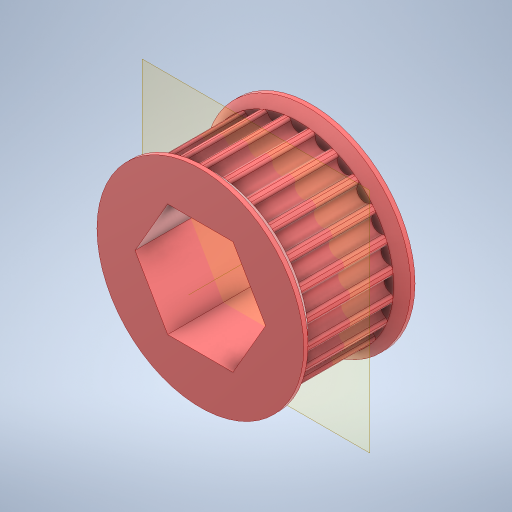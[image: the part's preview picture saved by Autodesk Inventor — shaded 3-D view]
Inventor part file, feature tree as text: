
AUTODESK INVENTOR PART (.ipt)
format: ipt  version: 2023.3 (Build 273359000, 359)  size: 504,832 bytes
history: native  units: in
note: dims shown in document units (in); Inventor stores cm internally (conversion verified against a paired STEP export)
features: sketch x7, extrude x6, mirror x2, chamfer x2, other x1, fillet x1, pattern_circular x1
ambient origin geometry x8: Origin, YZ Plane, XZ Plane, XY Plane, X Axis, Y Axis, Z Axis, Center Point
bodies: Solid1 (feature_tree)
feature tree (20):
  other  "Hex Bore"
  extrude  "HTD Base"  Depth=0.3937in TaperAngle=0.0deg
  extrude  "HTD Flange"  Depth=0.0591in
  mirror  "HTD Flanges"
  chamfer  "HTD Flange Chamfer"  Distance=0.0787in Angle=45.0deg
  extrude  "GT2 Base"  TaperAngle=0.0deg  [1 undecoded]
  extrude  "GT2 Base Tooth"  TaperAngle=0.0deg  [1 undecoded]
  fillet  "GT2 Base Tooth pt. 2"  Radius=0.8723in
  pattern_circular  "GT2 Teeth"  [2 undecoded]
  extrude  "GT2 Flange"  Depth=0.0591in
  mirror  "GT2 Flanges"
  chamfer  "GT2 Flange Chamfer"  Distance=0.0075in
  extrude  "Circle Bore"  TaperAngle=0.0deg  [1 undecoded]
  sketch  "Sketch1"  dims[d0=1.4588in d1=0.3937in d2=0.0in]
  sketch  "Sketch3"  dims[d12=0.0394in d13=0.0591in]
  sketch  "Sketch4"  dims[d14=0.0in]
  sketch  "Sketch5"  dims[d15=0.0394in d16=0.0787in d17=45.0deg]
  sketch  "Sketch6"  dims[d18=0.52in d19=0.0in d20=0.0in]
  sketch  "Sketch7"  dims[d21=0.52in d22=0.0in d23=0.0in d24=0.8723in]
  sketch  "Sketch8"  dims[d25=0.3937in d26=0.0in d27=0.0727in d28=0.0075in d29=0.0in d30=0.0in d31=0.0118in d32=9.4488in d33=360.0deg d35=0.0394in d36=0.0591in d37=0.0in d38=0.0394in d39=0.0787in d40=45.0deg]
note: 5 required parameter values undecoded (feature->parameter linkage not recoverable at this tier; creation-order binding heuristic only, values carry confidence <= 0.55)
